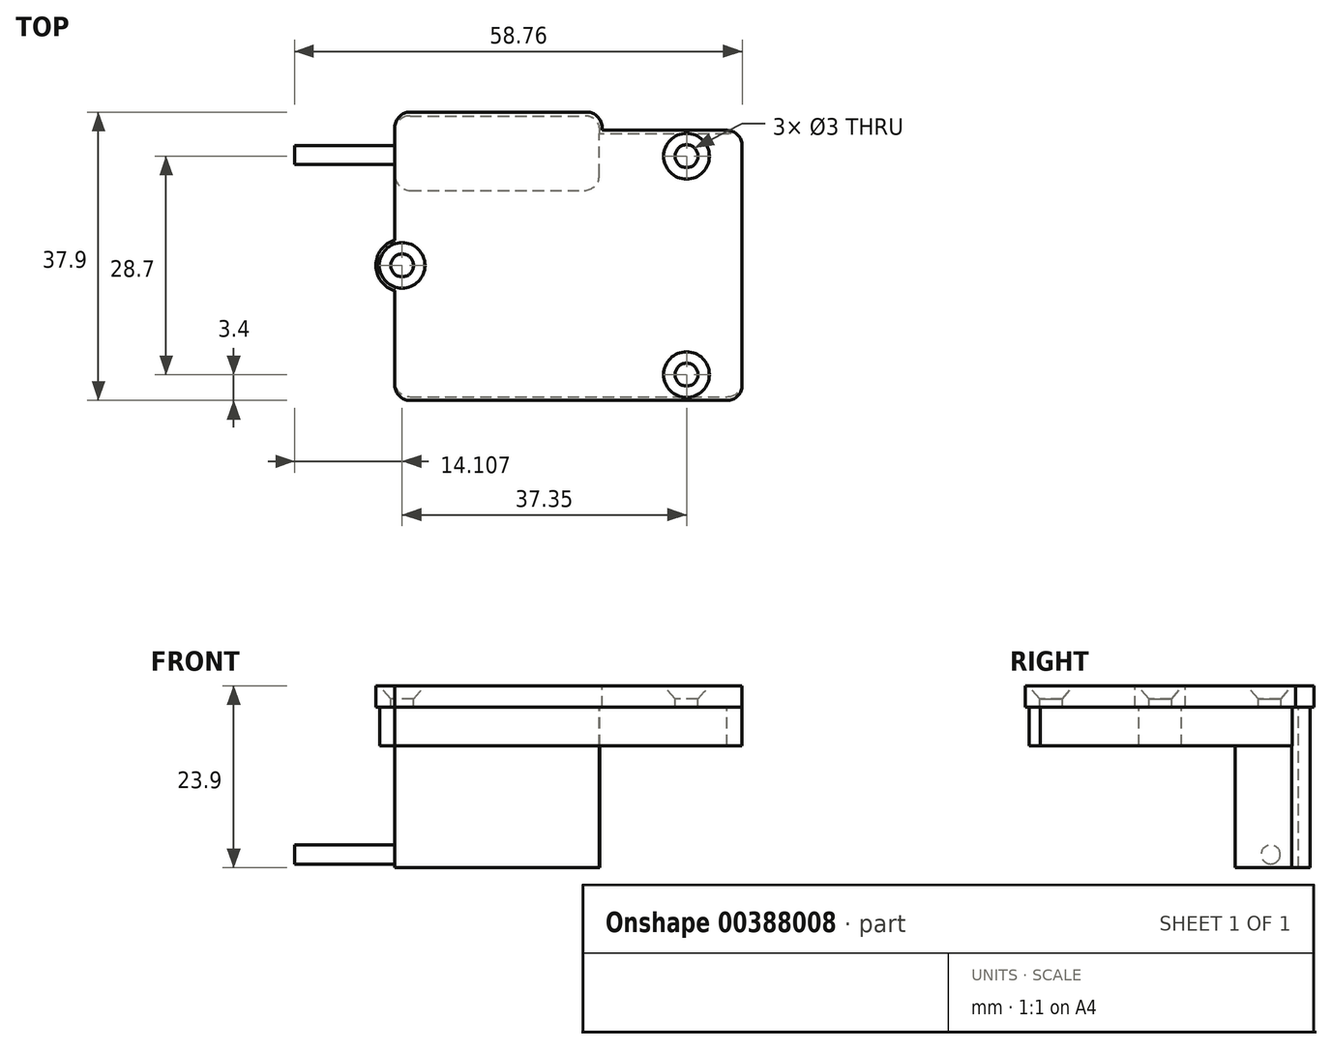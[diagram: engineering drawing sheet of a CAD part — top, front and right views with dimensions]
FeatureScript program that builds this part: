
annotation { "Feature Type Name" : "Feature", "Feature Type Description" : "" }
export const myFeature = defineFeature(function(context is Context, id is Id, definition is map)
    precondition{}
    {
        {
            var Q0;
            Q0=qCreatedBy(makeId("Top.planeOp"),FACE);
            var sketch = newSketch(context, id + "F0", { "sketchPlane" : qUnion([Q0])});
            skLineSegment(sketch, "E0.bottom", {"start": v(-23.95, 20.15) * mm, "end": v(-0.75, 20.15) * mm});
            skLineSegment(sketch, "E0.top", {"start": v(-23.95, -17.75) * mm, "end": v(17.65, -17.75) * mm});
            skLineSegment(sketch, "E0.left", {"start": v(-25.95, 18.15) * mm, "end": v(-25.95, 3.32) * mm});
            skLineSegment(sketch, "E0.right", {"start": v(19.65, 15.75) * mm, "end": v(19.65, -15.75) * mm});
            skPoint(sketch, "E1", {"position": v(1.25, 20.15) * mm});
            skLineSegment(sketch, "E2", {"start": v(17.65, 17.75) * mm, "end": v(1.25, 17.75) * mm});
            skLineSegment(sketch, "E3", {"start": v(1.25, 17.75) * mm, "end": v(1.25, 18.15) * mm});
            skArc(sketch, "E4", {"start": v(-25.95, 3.32) * mm, "mid": v(-28.45, 0) * mm, "end": v(-25.95, -3.32) * mm});
            skLineSegment(sketch, "E5.trimOffspring", {"start": v(-25.95, -3.32) * mm, "end": v(-25.95, -15.75) * mm});
            skLineSegment(sketch, "E6", {"start": v(12.35, 17.75) * mm, "end": v(12.35, 14.35) * mm, "construction": true});
            skPoint(sketch, "E7", {"position": v(12.35, 14.35) * mm});
            skPoint(sketch, "E8", {"position": v(12.35, -14.35) * mm});
            skLineSegment(sketch, "E9.trimOffspring", {"start": v(12.35, -14.35) * mm, "end": v(12.35, -17.75) * mm, "construction": true});
            skLineSegment(sketch, "E10", {"start": v(19.65, 0) * mm, "end": v(-25, 0) * mm, "construction": true});
            skPoint(sketch, "E11.visualSharp", {"position": v(-25.95, -17.75) * mm});
            skArc(sketch, "E11.filletArc", {"start": v(-25.95, -15.75) * mm, "mid": v(-25.37, -17.16) * mm, "end": v(-23.95, -17.75) * mm});
            skPoint(sketch, "E12.visualSharp", {"position": v(-25.95, 20.15) * mm});
            skArc(sketch, "E12.filletArc", {"start": v(-23.95, 20.15) * mm, "mid": v(-25.37, 19.56) * mm, "end": v(-25.95, 18.15) * mm});
            skPoint(sketch, "E13.visualSharp", {"position": v(19.65, 17.75) * mm});
            skArc(sketch, "E13.filletArc", {"start": v(19.65, 15.75) * mm, "mid": v(19.06, 17.16) * mm, "end": v(17.65, 17.75) * mm});
            skPoint(sketch, "E14.visualSharp", {"position": v(19.65, -17.75) * mm});
            skArc(sketch, "E14.filletArc", {"start": v(17.65, -17.75) * mm, "mid": v(19.06, -17.16) * mm, "end": v(19.65, -15.75) * mm});
            skArc(sketch, "E15.filletArc", {"start": v(1.25, 18.15) * mm, "mid": v(0.66, 19.56) * mm, "end": v(-0.75, 20.15) * mm});
            skSolve(sketch);
        }
        {
            var Q0;
            Q0 = qSketchRegion(id + "F0", true);
            extrude(context, id + "F1", {"entities" : qUnion([Q0]), "oppositeDirection" : true, "depth" : 2.8 * mm});
        }
        {
            var Q0;
            Q0=sQuery(id+"F0.wireOp",VERTEX,"E4.center");
            var Q1;
            Q1=sQuery(id+"F0.wireOp",VERTEX,"E7");
            var Q2;
            Q2=sQuery(id+"F0.wireOp",VERTEX,"E8");
            var Q3;
            Q3=makeQuery(id+"F1.opExtrude","SWEPT_BODY",BODY,{"disambiguationData":[OSD([sQuery(id+"F0.wireOp",EDGE,"E0.bottom"),sQuery(id+"F0.wireOp",EDGE,"E0.top"),sQuery(id+"F0.wireOp",EDGE,"E0.left"),sQuery(id+"F0.wireOp",EDGE,"E0.right"),sQuery(id+"F0.wireOp",EDGE,"E2"),sQuery(id+"F0.wireOp",EDGE,"E3"),sQuery(id+"F0.wireOp",EDGE,"E4"),sQuery(id+"F0.wireOp",EDGE,"E5.trimOffspring"),sQuery(id+"F0.wireOp",EDGE,"E11.filletArc"),sQuery(id+"F0.wireOp",EDGE,"E12.filletArc"),sQuery(id+"F0.wireOp",EDGE,"E13.filletArc"),sQuery(id+"F0.wireOp",EDGE,"E14.filletArc"),sQuery(id+"F0.wireOp",EDGE,"E15.filletArc")])]});
            hole(context, id + "F2", {"style" : HoleStyle.C_SINK, "endStyle" : HoleEndStyle.THROUGH, "standardTappedOrClearance" : lookupTablePath({ "standard" : "ISO", "size" : "3", "type" : "Drilled" }), "standardBlindInLast" : lookupTablePath({ "standard" : "ISO", "size" : "3", "type" : "Drilled" }), "holeDiameter" : 3 * mm, "cSinkDiameter" : 6 * mm, "cSinkAngle" : 82 * degree, "isTappedThrough" : true, "tappedDepth" : 12 * mm, "tapClearance" : 3, "startFromSketch" : true, "locations" : qUnion([Q0, Q1, Q2]), "scope" : qUnion([Q3])});
        }
        {
            var Q0;
            Q0=makeQuery(id+"F1.opExtrude","CAP_FACE",FACE,{"disambiguationData":[OSD([sQuery(id+"F0.wireOp",EDGE,"E0.bottom"),sQuery(id+"F0.wireOp",EDGE,"E0.top"),sQuery(id+"F0.wireOp",EDGE,"E0.left"),sQuery(id+"F0.wireOp",EDGE,"E0.right"),sQuery(id+"F0.wireOp",EDGE,"E2"),sQuery(id+"F0.wireOp",EDGE,"E3"),sQuery(id+"F0.wireOp",EDGE,"E4"),sQuery(id+"F0.wireOp",EDGE,"E5.trimOffspring"),sQuery(id+"F0.wireOp",EDGE,"E11.filletArc"),sQuery(id+"F0.wireOp",EDGE,"E12.filletArc"),sQuery(id+"F0.wireOp",EDGE,"E13.filletArc"),sQuery(id+"F0.wireOp",EDGE,"E14.filletArc"),sQuery(id+"F0.wireOp",EDGE,"E15.filletArc")])],"isStart":false});
            var sketch = newSketch(context, id + "F3", { "sketchPlane" : qUnion([Q0])});
            skLineSegment(sketch, "E16.0", {"start": v(-23.95, 17.25) * mm, "end": v(17.65, 17.25) * mm});
            skLineSegment(sketch, "E17.0", {"start": v(-23.95, -19.65) * mm, "end": v(-0.96, -19.65) * mm});
            skLineSegment(sketch, "E18.0", {"start": v(17.65, -17.25) * mm, "end": v(0.9, -17.25) * mm});
            skArc(sketch, "E19", {"start": v(-0.96, -19.65) * mm, "mid": v(0.55, -18.9) * mm, "end": v(0.9, -17.25) * mm});
            skLineSegment(sketch, "E20.0", {"start": v(-25.95, -18.15) * mm, "end": v(-25.95, -3.32) * mm});
            skLineSegment(sketch, "E21.0", {"start": v(-25.95, 3.32) * mm, "end": v(-25.95, 15.75) * mm});
            skArc(sketch, "E22.0", {"start": v(-25.95, -2.8) * mm, "mid": v(-27.95, 0) * mm, "end": v(-25.95, 2.8) * mm});
            skLineSegment(sketch, "E23", {"start": v(-25.95, -2.8) * mm, "end": v(-25.95, -3.32) * mm});
            skLineSegment(sketch, "E24", {"start": v(-25.95, 3.32) * mm, "end": v(-25.95, 2.8) * mm});
            skArc(sketch, "E25", {"start": v(-23.95, -19.65) * mm, "mid": v(-25.2, -19.23) * mm, "end": v(-25.95, -18.15) * mm});
            skArc(sketch, "E26", {"start": v(-23.95, 17.25) * mm, "mid": v(-25.2, 16.83) * mm, "end": v(-25.95, 15.75) * mm});
            skLineSegment(sketch, "E27.0", {"start": v(19.65, -15.75) * mm, "end": v(19.65, 15.75) * mm});
            skArc(sketch, "E28", {"start": v(17.65, 17.25) * mm, "mid": v(18.9, 16.83) * mm, "end": v(19.65, 15.75) * mm});
            skArc(sketch, "E29", {"start": v(19.65, -15.75) * mm, "mid": v(19.02, -17) * mm, "end": v(17.65, -17.25) * mm});
            skSolve(sketch);
        }
        {
            var Q0;
            Q0 = qSketchRegion(id + "F3", true);
            extrude(context, id + "F4", {"entities" : qUnion([Q0]), "depth" : 5.1 * mm});
        }
        {
            var Q0;
            Q0=makeQuery(id+"F4.opExtrude","CAP_FACE",FACE,{"disambiguationData":[OSD([sQuery(id+"F3.wireOp",EDGE,"E16.0"),sQuery(id+"F3.wireOp",EDGE,"E17.0"),sQuery(id+"F3.wireOp",EDGE,"E18.0"),sQuery(id+"F3.wireOp",EDGE,"E19"),sQuery(id+"F3.wireOp",EDGE,"E20.0"),sQuery(id+"F3.wireOp",EDGE,"E21.0"),sQuery(id+"F3.wireOp",EDGE,"E22.0"),sQuery(id+"F3.wireOp",EDGE,"E23"),sQuery(id+"F3.wireOp",EDGE,"E24"),sQuery(id+"F3.wireOp",EDGE,"E25"),sQuery(id+"F3.wireOp",EDGE,"E26"),sQuery(id+"F3.wireOp",EDGE,"E27.0"),sQuery(id+"F3.wireOp",EDGE,"E28"),sQuery(id+"F3.wireOp",EDGE,"E29")])],"isStart":false});
            var sketch = newSketch(context, id + "F5", { "sketchPlane" : qUnion([Q0])});
            skLineSegment(sketch, "E30", {"start": v(-25.95, -18.15) * mm, "end": v(-25.95, -11.85) * mm});
            skLineSegment(sketch, "E31", {"start": v(-23.95, -9.85) * mm, "end": v(-1.1, -9.85) * mm});
            skLineSegment(sketch, "E32", {"start": v(0.9, -11.85) * mm, "end": v(0.9, -17.25) * mm});
            skPoint(sketch, "E33.visualSharp", {"position": v(-25.95, -9.85) * mm});
            skArc(sketch, "E33.filletArc", {"start": v(-23.95, -9.85) * mm, "mid": v(-25.37, -10.44) * mm, "end": v(-25.95, -11.85) * mm});
            skPoint(sketch, "E34.visualSharp", {"position": v(0.9, -9.85) * mm});
            skArc(sketch, "E34.filletArc", {"start": v(0.9, -11.85) * mm, "mid": v(0.3, -10.44) * mm, "end": v(-1.1, -9.85) * mm});
            skSolve(sketch);
        }
        {
            var Q0;
            Q0=makeQuery(id+"F5.imprint","IMPRINT",FACE,{"disambiguationData":[TD([[makeQuery(id+"F5.imprint","IMPRINT",EDGE,{"derivedFrom":sQuery(id+"F5.wireOp",EDGE,"E30")}),1.0]])]});
            extrude(context, id + "F6", {"entities" : qUnion([Q0]), "operationType" : NewBodyOperationType.ADD, "depth" : 16 * mm});
        }
        {
            var Q0;
            Q0=makeQuery(id+"F6.opExtrude","SWEPT_FACE",FACE,{"disambiguationData":[OSD([sQuery(id+"F5.wireOp",EDGE,"E32")])]});
            var sketch = newSketch(context, id + "F7", { "sketchPlane" : qUnion([Q0])});
            skCircle(sketch, "E35", {"center": v(14.5, -22.15) * mm, "radius": 1.25 * mm});
            skSolve(sketch);
        }
        {
            var Q0;
            Q0=makeQuery(id+"F7.imprint","IMPRINT",FACE,{"disambiguationData":[TD([[makeQuery(id+"F7.imprint","IMPRINT",EDGE,{"derivedFrom":sQuery(id+"F7.wireOp",EDGE,"E35")}),1.0]])]});
            extrude(context, id + "F8", {"entities" : qUnion([Q0]), "operationType" : NewBodyOperationType.ADD, "oppositeDirection" : true, "depth" : 40 * mm});
        }
    });
